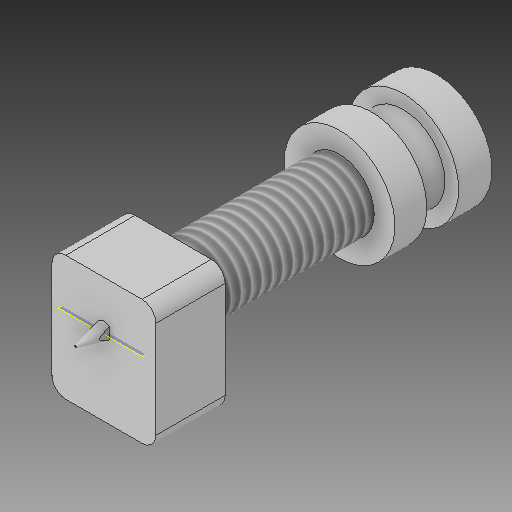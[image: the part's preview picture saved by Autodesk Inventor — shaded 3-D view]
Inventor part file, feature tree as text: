
AUTODESK INVENTOR PART (.ipt)
format: ipt  version: 2018 (Build 220112000, 112)  size: 190,976 bytes
history: native  units: mm
features: sketch x10, other x3, plane x1
ambient origin geometry x8: Origin, YZ Plane, XZ Plane, XY Plane, X Axis, Y Axis, Z Axis, Center Point
bodies: Solid1 (feature_tree)
feature tree (14):
  other  "Hotend Mock Up.ipt"
  other  "Solid1::Hotend Mock Up.ipt"
  other  "TaggingFeature1"
  sketch  "Sketch1"  dims[d0=10.0mm]
  sketch  "Sketch2"
  sketch  "Sketch3"
  sketch  "Sketch4"
  sketch  "Sketch5"
  sketch  "Sketch6"
  sketch  "Sketch7"
  sketch  "Sketch8"
  sketch  "Sketch9"
  sketch  "Sketch10"
  plane  "Work Plane1"
